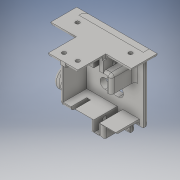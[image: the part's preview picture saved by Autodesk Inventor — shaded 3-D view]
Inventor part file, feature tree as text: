
AUTODESK INVENTOR PART (.ipt)
format: ipt  version: 2016 (Build 200138000, 138)  size: 609,280 bytes
history: native  units: in
note: dims shown in document units (in); Inventor stores cm internally (conversion verified against a paired STEP export)
features: sketch x17, other x3
ambient origin geometry x8: Origin, YZ Plane, XZ Plane, XY Plane, X Axis, Y Axis, Z Axis, Center Point
bodies: Solid1 (feature_tree)
feature tree (20):
  other  "Knee_holder_v3.ipt"
  other  "Solid1::Knee_holder_v3.ipt"
  other  "TaggingFeature1"
  sketch  "Sketch1"  dims[d0=0.3937in]
  sketch  "Sketch12"
  sketch  "Sketch22"
  sketch  "Sketch32"
  sketch  "Sketch35"
  sketch  "Sketch36"
  sketch  "Sketch41"
  sketch  "Sketch43"
  sketch  "Sketch46"
  sketch  "Sketch47"
  sketch  "Sketch48"
  sketch  "Sketch49"
  sketch  "Sketch50"
  sketch  "Sketch51"
  sketch  "Sketch52"
  sketch  "Sketch53"
  sketch  "Sketch54"
